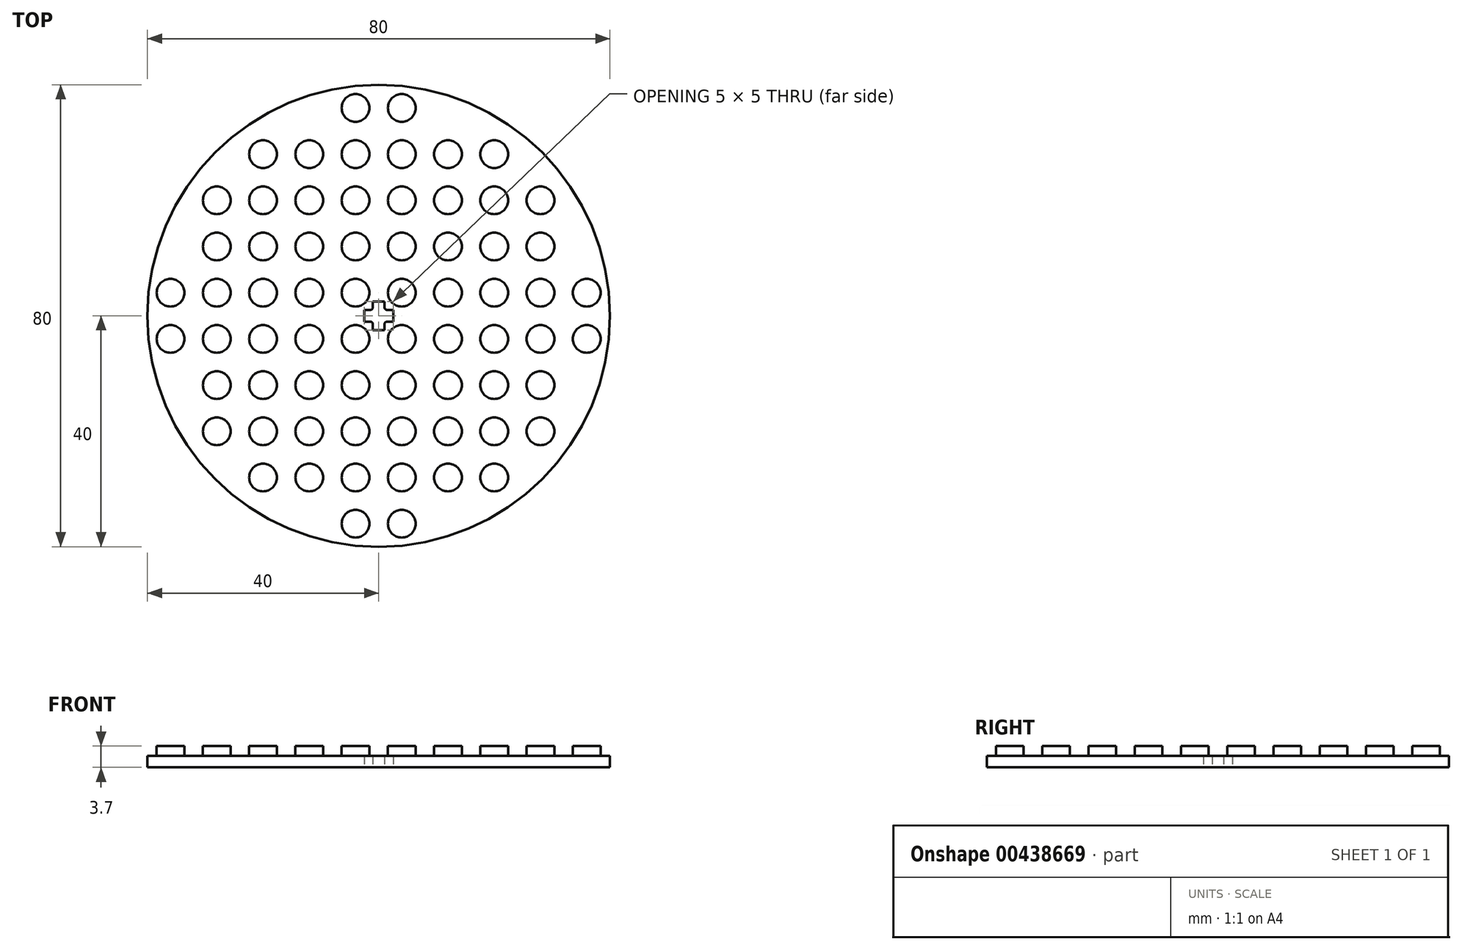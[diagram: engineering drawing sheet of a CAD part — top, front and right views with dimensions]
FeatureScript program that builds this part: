
annotation { "Feature Type Name" : "Feature", "Feature Type Description" : "" }
export const myFeature = defineFeature(function(context is Context, id is Id, definition is map)
    precondition{}
    {
        {
            var Q0;
            Q0=qCreatedBy(makeId("Top.planeOp"),FACE);
            var sketch = newSketch(context, id + "F0", { "sketchPlane" : qUnion([Q0])});
            skCircle(sketch, "E0", {"center": v(0, 0) * mm, "radius": 2.4 * mm});
            skCircle(sketch, "E1.0.1.0", {"center": v(0, 8) * mm, "radius": 2.4 * mm});
            skCircle(sketch, "E1.0.4.0", {"center": v(0, 32) * mm, "radius": 2.4 * mm});
            skCircle(sketch, "E1.0.5.0", {"center": v(0, 40) * mm, "radius": 2.4 * mm});
            skCircle(sketch, "E1.1.0.0", {"center": v(8, 0) * mm, "radius": 2.4 * mm});
            skCircle(sketch, "E1.1.2.0", {"center": v(8, 16) * mm, "radius": 2.4 * mm});
            skCircle(sketch, "E1.1.3.0", {"center": v(8, 24) * mm, "radius": 2.4 * mm});
            skCircle(sketch, "E1.1.4.0", {"center": v(8, 32) * mm, "radius": 2.4 * mm});
            skCircle(sketch, "E1.1.5.0", {"center": v(8, 40) * mm, "radius": 2.4 * mm});
            skCircle(sketch, "E1.1.6.0", {"center": v(8, 48) * mm, "radius": 2.4 * mm});
            skCircle(sketch, "E1.1.7.0", {"center": v(8, 56) * mm, "radius": 2.4 * mm});
            skCircle(sketch, "E1.2.1.0", {"center": v(16, 8) * mm, "radius": 2.4 * mm});
            skCircle(sketch, "E1.2.2.0", {"center": v(16, 16) * mm, "radius": 2.4 * mm});
            skCircle(sketch, "E1.2.3.0", {"center": v(16, 24) * mm, "radius": 2.4 * mm});
            skCircle(sketch, "E1.2.4.0", {"center": v(16, 32) * mm, "radius": 2.4 * mm});
            skCircle(sketch, "E1.2.5.0", {"center": v(16, 40) * mm, "radius": 2.4 * mm});
            skCircle(sketch, "E1.2.6.0", {"center": v(16, 48) * mm, "radius": 2.4 * mm});
            skCircle(sketch, "E1.2.7.0", {"center": v(16, 56) * mm, "radius": 2.4 * mm});
            skCircle(sketch, "E1.2.8.0", {"center": v(16, 64) * mm, "radius": 2.4 * mm});
            skCircle(sketch, "E1.3.1.0", {"center": v(24, 8) * mm, "radius": 2.4 * mm});
            skCircle(sketch, "E1.3.2.0", {"center": v(24, 16) * mm, "radius": 2.4 * mm});
            skCircle(sketch, "E1.3.3.0", {"center": v(24, 24) * mm, "radius": 2.4 * mm});
            skCircle(sketch, "E1.3.4.0", {"center": v(24, 32) * mm, "radius": 2.4 * mm});
            skCircle(sketch, "E1.3.5.0", {"center": v(24, 40) * mm, "radius": 2.4 * mm});
            skCircle(sketch, "E1.3.6.0", {"center": v(24, 48) * mm, "radius": 2.4 * mm});
            skCircle(sketch, "E1.3.7.0", {"center": v(24, 56) * mm, "radius": 2.4 * mm});
            skCircle(sketch, "E1.3.8.0", {"center": v(24, 64) * mm, "radius": 2.4 * mm});
            skCircle(sketch, "E1.4.0.0", {"center": v(32, 0) * mm, "radius": 2.4 * mm});
            skCircle(sketch, "E1.4.1.0", {"center": v(32, 8) * mm, "radius": 2.4 * mm});
            skCircle(sketch, "E1.4.2.0", {"center": v(32, 16) * mm, "radius": 2.4 * mm});
            skCircle(sketch, "E1.4.3.0", {"center": v(32, 24) * mm, "radius": 2.4 * mm});
            skCircle(sketch, "E1.4.4.0", {"center": v(32, 32) * mm, "radius": 2.4 * mm});
            skCircle(sketch, "E1.4.5.0", {"center": v(32, 40) * mm, "radius": 2.4 * mm});
            skCircle(sketch, "E1.4.6.0", {"center": v(32, 48) * mm, "radius": 2.4 * mm});
            skCircle(sketch, "E1.4.7.0", {"center": v(32, 56) * mm, "radius": 2.4 * mm});
            skCircle(sketch, "E1.4.8.0", {"center": v(32, 64) * mm, "radius": 2.4 * mm});
            skCircle(sketch, "E1.4.9.0", {"center": v(32, 72) * mm, "radius": 2.4 * mm});
            skCircle(sketch, "E1.5.0.0", {"center": v(40, 0) * mm, "radius": 2.4 * mm});
            skCircle(sketch, "E1.5.1.0", {"center": v(40, 8) * mm, "radius": 2.4 * mm});
            skCircle(sketch, "E1.5.2.0", {"center": v(40, 16) * mm, "radius": 2.4 * mm});
            skCircle(sketch, "E1.5.3.0", {"center": v(40, 24) * mm, "radius": 2.4 * mm});
            skCircle(sketch, "E1.5.4.0", {"center": v(40, 32) * mm, "radius": 2.4 * mm});
            skCircle(sketch, "E1.5.5.0", {"center": v(40, 40) * mm, "radius": 2.4 * mm});
            skCircle(sketch, "E1.5.6.0", {"center": v(40, 48) * mm, "radius": 2.4 * mm});
            skCircle(sketch, "E1.5.7.0", {"center": v(40, 56) * mm, "radius": 2.4 * mm});
            skCircle(sketch, "E1.5.8.0", {"center": v(40, 64) * mm, "radius": 2.4 * mm});
            skCircle(sketch, "E1.5.9.0", {"center": v(40, 72) * mm, "radius": 2.4 * mm});
            skCircle(sketch, "E1.6.1.0", {"center": v(48, 8) * mm, "radius": 2.4 * mm});
            skCircle(sketch, "E1.6.2.0", {"center": v(48, 16) * mm, "radius": 2.4 * mm});
            skCircle(sketch, "E1.6.3.0", {"center": v(48, 24) * mm, "radius": 2.4 * mm});
            skCircle(sketch, "E1.6.4.0", {"center": v(48, 32) * mm, "radius": 2.4 * mm});
            skCircle(sketch, "E1.6.5.0", {"center": v(48, 40) * mm, "radius": 2.4 * mm});
            skCircle(sketch, "E1.6.6.0", {"center": v(48, 48) * mm, "radius": 2.4 * mm});
            skCircle(sketch, "E1.6.7.0", {"center": v(48, 56) * mm, "radius": 2.4 * mm});
            skCircle(sketch, "E1.6.8.0", {"center": v(48, 64) * mm, "radius": 2.4 * mm});
            skCircle(sketch, "E1.7.1.0", {"center": v(56, 8) * mm, "radius": 2.4 * mm});
            skCircle(sketch, "E1.7.2.0", {"center": v(56, 16) * mm, "radius": 2.4 * mm});
            skCircle(sketch, "E1.7.3.0", {"center": v(56, 24) * mm, "radius": 2.4 * mm});
            skCircle(sketch, "E1.7.4.0", {"center": v(56, 32) * mm, "radius": 2.4 * mm});
            skCircle(sketch, "E1.7.5.0", {"center": v(56, 40) * mm, "radius": 2.4 * mm});
            skCircle(sketch, "E1.7.6.0", {"center": v(56, 48) * mm, "radius": 2.4 * mm});
            skCircle(sketch, "E1.7.7.0", {"center": v(56, 56) * mm, "radius": 2.4 * mm});
            skCircle(sketch, "E1.7.8.0", {"center": v(56, 64) * mm, "radius": 2.4 * mm});
            skCircle(sketch, "E1.8.2.0", {"center": v(64, 16) * mm, "radius": 2.4 * mm});
            skCircle(sketch, "E1.8.3.0", {"center": v(64, 24) * mm, "radius": 2.4 * mm});
            skCircle(sketch, "E1.8.4.0", {"center": v(64, 32) * mm, "radius": 2.4 * mm});
            skCircle(sketch, "E1.8.5.0", {"center": v(64, 40) * mm, "radius": 2.4 * mm});
            skCircle(sketch, "E1.8.6.0", {"center": v(64, 48) * mm, "radius": 2.4 * mm});
            skCircle(sketch, "E1.8.7.0", {"center": v(64, 56) * mm, "radius": 2.4 * mm});
            skCircle(sketch, "E1.9.4.0", {"center": v(72, 32) * mm, "radius": 2.4 * mm});
            skCircle(sketch, "E1.9.5.0", {"center": v(72, 40) * mm, "radius": 2.4 * mm});
            skLineSegment(sketch, "E1.direction1", {"start": v(0, 0) * mm, "end": v(8, 0) * mm, "construction": true});
            skLineSegment(sketch, "E1.direction2", {"start": v(0, 0) * mm, "end": v(0, 8) * mm, "construction": true});
            skLineSegment(sketch, "E2", {"start": v(40, 32) * mm, "end": v(32, 40) * mm, "construction": true});
            skLineSegment(sketch, "E3", {"start": v(40, 40) * mm, "end": v(32, 32) * mm, "construction": true});
            skCircle(sketch, "E4", {"center": v(36, 36) * mm, "radius": 40 * mm});
            skLineSegment(sketch, "E5.bottom", {"start": v(35, 33.5) * mm, "end": v(37, 33.5) * mm});
            skLineSegment(sketch, "E5.top", {"start": v(35, 38.5) * mm, "end": v(37, 38.5) * mm});
            skLineSegment(sketch, "E5.left", {"start": v(35, 33.5) * mm, "end": v(35, 38.5) * mm});
            skLineSegment(sketch, "E5.right", {"start": v(37, 33.5) * mm, "end": v(37, 38.5) * mm});
            skLineSegment(sketch, "E6.bottom", {"start": v(38.5, 35) * mm, "end": v(33.5, 35) * mm});
            skLineSegment(sketch, "E6.top", {"start": v(38.5, 37) * mm, "end": v(35, 37) * mm});
            skLineSegment(sketch, "E6.left", {"start": v(38.5, 35) * mm, "end": v(38.5, 37) * mm});
            skLineSegment(sketch, "E6.right", {"start": v(33.5, 35) * mm, "end": v(33.5, 37) * mm});
            skLineSegment(sketch, "E7", {"start": v(35, 37) * mm, "end": v(33.5, 37) * mm});
            skSolve(sketch);
        }
        {
            var Q0;
            Q0=makeQuery(id+"F0.imprint","IMPRINT",FACE,{"disambiguationData":[TD([[makeQuery(id+"F0.imprint","IMPRINT",EDGE,{"derivedFrom":sQuery(id+"F0.wireOp",EDGE,"E1.1.2.0")}),1.0]])]});
            var Q1;
            Q1=makeQuery(id+"F0.imprint","IMPRINT",FACE,{"disambiguationData":[TD([[makeQuery(id+"F0.imprint","IMPRINT",EDGE,{"derivedFrom":sQuery(id+"F0.wireOp",EDGE,"E1.2.1.0")}),1.0]])]});
            var Q2;
            Q2=makeQuery(id+"F0.imprint","IMPRINT",FACE,{"disambiguationData":[TD([[makeQuery(id+"F0.imprint","IMPRINT",EDGE,{"derivedFrom":sQuery(id+"F0.wireOp",EDGE,"E1.3.1.0")}),1.0]])]});
            var Q3;
            Q3=makeQuery(id+"F0.imprint","IMPRINT",FACE,{"disambiguationData":[TD([[makeQuery(id+"F0.imprint","IMPRINT",EDGE,{"derivedFrom":sQuery(id+"F0.wireOp",EDGE,"E1.2.2.0")}),1.0]])]});
            var Q4;
            Q4=makeQuery(id+"F0.imprint","IMPRINT",FACE,{"disambiguationData":[TD([[makeQuery(id+"F0.imprint","IMPRINT",EDGE,{"derivedFrom":sQuery(id+"F0.wireOp",EDGE,"E1.3.2.0")}),1.0]])]});
            var Q5;
            Q5=makeQuery(id+"F0.imprint","IMPRINT",FACE,{"disambiguationData":[TD([[makeQuery(id+"F0.imprint","IMPRINT",EDGE,{"derivedFrom":sQuery(id+"F0.wireOp",EDGE,"E1.4.0.0")}),1.0]])]});
            var Q6;
            Q6=makeQuery(id+"F0.imprint","IMPRINT",FACE,{"disambiguationData":[TD([[makeQuery(id+"F0.imprint","IMPRINT",EDGE,{"derivedFrom":sQuery(id+"F0.wireOp",EDGE,"E1.4.1.0")}),1.0]])]});
            var Q7;
            Q7=makeQuery(id+"F0.imprint","IMPRINT",FACE,{"disambiguationData":[TD([[makeQuery(id+"F0.imprint","IMPRINT",EDGE,{"derivedFrom":sQuery(id+"F0.wireOp",EDGE,"E1.4.2.0")}),1.0]])]});
            var Q8;
            Q8=makeQuery(id+"F0.imprint","IMPRINT",FACE,{"disambiguationData":[TD([[makeQuery(id+"F0.imprint","IMPRINT",EDGE,{"derivedFrom":sQuery(id+"F0.wireOp",EDGE,"E1.4.3.0")}),1.0]])]});
            var Q9;
            Q9=makeQuery(id+"F0.imprint","IMPRINT",FACE,{"disambiguationData":[TD([[makeQuery(id+"F0.imprint","IMPRINT",EDGE,{"derivedFrom":sQuery(id+"F0.wireOp",EDGE,"E1.3.3.0")}),1.0]])]});
            var Q10;
            Q10=makeQuery(id+"F0.imprint","IMPRINT",FACE,{"disambiguationData":[TD([[makeQuery(id+"F0.imprint","IMPRINT",EDGE,{"derivedFrom":sQuery(id+"F0.wireOp",EDGE,"E1.2.3.0")}),1.0]])]});
            var Q11;
            Q11=makeQuery(id+"F0.imprint","IMPRINT",FACE,{"disambiguationData":[TD([[makeQuery(id+"F0.imprint","IMPRINT",EDGE,{"derivedFrom":sQuery(id+"F0.wireOp",EDGE,"E1.1.3.0")}),1.0]])]});
            var Q12;
            Q12=makeQuery(id+"F0.imprint","IMPRINT",FACE,{"disambiguationData":[TD([[makeQuery(id+"F0.imprint","IMPRINT",EDGE,{"derivedFrom":sQuery(id+"F0.wireOp",EDGE,"E1.0.4.0")}),1.0]])]});
            var Q13;
            Q13=makeQuery(id+"F0.imprint","IMPRINT",FACE,{"disambiguationData":[TD([[makeQuery(id+"F0.imprint","IMPRINT",EDGE,{"derivedFrom":sQuery(id+"F0.wireOp",EDGE,"E1.1.4.0")}),1.0]])]});
            var Q14;
            Q14=makeQuery(id+"F0.imprint","IMPRINT",FACE,{"disambiguationData":[TD([[makeQuery(id+"F0.imprint","IMPRINT",EDGE,{"derivedFrom":sQuery(id+"F0.wireOp",EDGE,"E1.2.4.0")}),1.0]])]});
            var Q15;
            Q15=makeQuery(id+"F0.imprint","IMPRINT",FACE,{"disambiguationData":[TD([[makeQuery(id+"F0.imprint","IMPRINT",EDGE,{"derivedFrom":sQuery(id+"F0.wireOp",EDGE,"E1.3.4.0")}),1.0]])]});
            var Q16;
            Q16=makeQuery(id+"F0.imprint","IMPRINT",FACE,{"disambiguationData":[TD([[makeQuery(id+"F0.imprint","IMPRINT",EDGE,{"derivedFrom":sQuery(id+"F0.wireOp",EDGE,"E1.4.4.0")}),1.0]])]});
            var Q17;
            Q17=makeQuery(id+"F0.imprint","IMPRINT",FACE,{"disambiguationData":[TD([[makeQuery(id+"F0.imprint","IMPRINT",EDGE,{"derivedFrom":sQuery(id+"F0.wireOp",EDGE,"E1.4.5.0")}),1.0]])]});
            var Q18;
            Q18=makeQuery(id+"F0.imprint","IMPRINT",FACE,{"disambiguationData":[TD([[makeQuery(id+"F0.imprint","IMPRINT",EDGE,{"derivedFrom":sQuery(id+"F0.wireOp",EDGE,"E1.3.5.0")}),1.0]])]});
            var Q19;
            Q19=makeQuery(id+"F0.imprint","IMPRINT",FACE,{"disambiguationData":[TD([[makeQuery(id+"F0.imprint","IMPRINT",EDGE,{"derivedFrom":sQuery(id+"F0.wireOp",EDGE,"E1.2.5.0")}),1.0]])]});
            var Q20;
            Q20=makeQuery(id+"F0.imprint","IMPRINT",FACE,{"disambiguationData":[TD([[makeQuery(id+"F0.imprint","IMPRINT",EDGE,{"derivedFrom":sQuery(id+"F0.wireOp",EDGE,"E1.1.5.0")}),1.0]])]});
            var Q21;
            Q21=makeQuery(id+"F0.imprint","IMPRINT",FACE,{"disambiguationData":[TD([[makeQuery(id+"F0.imprint","IMPRINT",EDGE,{"derivedFrom":sQuery(id+"F0.wireOp",EDGE,"E1.0.5.0")}),1.0]])]});
            var Q22;
            Q22=makeQuery(id+"F0.imprint","IMPRINT",FACE,{"disambiguationData":[TD([[makeQuery(id+"F0.imprint","IMPRINT",EDGE,{"derivedFrom":sQuery(id+"F0.wireOp",EDGE,"E1.1.6.0")}),1.0]])]});
            var Q23;
            Q23=makeQuery(id+"F0.imprint","IMPRINT",FACE,{"disambiguationData":[TD([[makeQuery(id+"F0.imprint","IMPRINT",EDGE,{"derivedFrom":sQuery(id+"F0.wireOp",EDGE,"E1.2.6.0")}),1.0]])]});
            var Q24;
            Q24=makeQuery(id+"F0.imprint","IMPRINT",FACE,{"disambiguationData":[TD([[makeQuery(id+"F0.imprint","IMPRINT",EDGE,{"derivedFrom":sQuery(id+"F0.wireOp",EDGE,"E1.4.6.0")}),1.0]])]});
            var Q25;
            Q25=makeQuery(id+"F0.imprint","IMPRINT",FACE,{"disambiguationData":[TD([[makeQuery(id+"F0.imprint","IMPRINT",EDGE,{"derivedFrom":sQuery(id+"F0.wireOp",EDGE,"E1.4.7.0")}),1.0]])]});
            var Q26;
            Q26=makeQuery(id+"F0.imprint","IMPRINT",FACE,{"disambiguationData":[TD([[makeQuery(id+"F0.imprint","IMPRINT",EDGE,{"derivedFrom":sQuery(id+"F0.wireOp",EDGE,"E1.3.7.0")}),1.0]])]});
            var Q27;
            Q27=makeQuery(id+"F0.imprint","IMPRINT",FACE,{"disambiguationData":[TD([[makeQuery(id+"F0.imprint","IMPRINT",EDGE,{"derivedFrom":sQuery(id+"F0.wireOp",EDGE,"E1.2.7.0")}),1.0]])]});
            var Q28;
            Q28=makeQuery(id+"F0.imprint","IMPRINT",FACE,{"disambiguationData":[TD([[makeQuery(id+"F0.imprint","IMPRINT",EDGE,{"derivedFrom":sQuery(id+"F0.wireOp",EDGE,"E1.1.7.0")}),1.0]])]});
            var Q29;
            Q29=makeQuery(id+"F0.imprint","IMPRINT",FACE,{"disambiguationData":[TD([[makeQuery(id+"F0.imprint","IMPRINT",EDGE,{"derivedFrom":sQuery(id+"F0.wireOp",EDGE,"E1.3.6.0")}),1.0]])]});
            var Q30;
            Q30=makeQuery(id+"F0.imprint","IMPRINT",FACE,{"disambiguationData":[TD([[makeQuery(id+"F0.imprint","IMPRINT",EDGE,{"derivedFrom":sQuery(id+"F0.wireOp",EDGE,"E1.2.8.0")}),1.0]])]});
            var Q31;
            Q31=makeQuery(id+"F0.imprint","IMPRINT",FACE,{"disambiguationData":[TD([[makeQuery(id+"F0.imprint","IMPRINT",EDGE,{"derivedFrom":sQuery(id+"F0.wireOp",EDGE,"E1.3.8.0")}),1.0]])]});
            var Q32;
            Q32=makeQuery(id+"F0.imprint","IMPRINT",FACE,{"disambiguationData":[TD([[makeQuery(id+"F0.imprint","IMPRINT",EDGE,{"derivedFrom":sQuery(id+"F0.wireOp",EDGE,"E1.4.8.0")}),1.0]])]});
            var Q33;
            Q33=makeQuery(id+"F0.imprint","IMPRINT",FACE,{"disambiguationData":[TD([[makeQuery(id+"F0.imprint","IMPRINT",EDGE,{"derivedFrom":sQuery(id+"F0.wireOp",EDGE,"E1.4.9.0")}),1.0]])]});
            var Q34;
            Q34=makeQuery(id+"F0.imprint","IMPRINT",FACE,{"disambiguationData":[TD([[makeQuery(id+"F0.imprint","IMPRINT",EDGE,{"derivedFrom":sQuery(id+"F0.wireOp",EDGE,"E1.5.9.0")}),1.0]])]});
            var Q35;
            Q35=makeQuery(id+"F0.imprint","IMPRINT",FACE,{"disambiguationData":[TD([[makeQuery(id+"F0.imprint","IMPRINT",EDGE,{"derivedFrom":sQuery(id+"F0.wireOp",EDGE,"E1.5.8.0")}),1.0]])]});
            var Q36;
            Q36=makeQuery(id+"F0.imprint","IMPRINT",FACE,{"disambiguationData":[TD([[makeQuery(id+"F0.imprint","IMPRINT",EDGE,{"derivedFrom":sQuery(id+"F0.wireOp",EDGE,"E1.5.7.0")}),1.0]])]});
            var Q37;
            Q37=makeQuery(id+"F0.imprint","IMPRINT",FACE,{"disambiguationData":[TD([[makeQuery(id+"F0.imprint","IMPRINT",EDGE,{"derivedFrom":sQuery(id+"F0.wireOp",EDGE,"E1.5.6.0")}),1.0]])]});
            var Q38;
            Q38=makeQuery(id+"F0.imprint","IMPRINT",FACE,{"disambiguationData":[TD([[makeQuery(id+"F0.imprint","IMPRINT",EDGE,{"derivedFrom":sQuery(id+"F0.wireOp",EDGE,"E1.5.5.0")}),1.0]])]});
            var Q39;
            Q39=makeQuery(id+"F0.imprint","IMPRINT",FACE,{"disambiguationData":[TD([[makeQuery(id+"F0.imprint","IMPRINT",EDGE,{"derivedFrom":sQuery(id+"F0.wireOp",EDGE,"E1.5.4.0")}),1.0]])]});
            var Q40;
            Q40=makeQuery(id+"F0.imprint","IMPRINT",FACE,{"disambiguationData":[TD([[makeQuery(id+"F0.imprint","IMPRINT",EDGE,{"derivedFrom":sQuery(id+"F0.wireOp",EDGE,"E1.5.3.0")}),1.0]])]});
            var Q41;
            Q41=makeQuery(id+"F0.imprint","IMPRINT",FACE,{"disambiguationData":[TD([[makeQuery(id+"F0.imprint","IMPRINT",EDGE,{"derivedFrom":sQuery(id+"F0.wireOp",EDGE,"E1.5.2.0")}),1.0]])]});
            var Q42;
            Q42=makeQuery(id+"F0.imprint","IMPRINT",FACE,{"disambiguationData":[TD([[makeQuery(id+"F0.imprint","IMPRINT",EDGE,{"derivedFrom":sQuery(id+"F0.wireOp",EDGE,"E1.5.1.0")}),1.0]])]});
            var Q43;
            Q43=makeQuery(id+"F0.imprint","IMPRINT",FACE,{"disambiguationData":[TD([[makeQuery(id+"F0.imprint","IMPRINT",EDGE,{"derivedFrom":sQuery(id+"F0.wireOp",EDGE,"E1.5.0.0")}),1.0]])]});
            var Q44;
            Q44=makeQuery(id+"F0.imprint","IMPRINT",FACE,{"disambiguationData":[TD([[makeQuery(id+"F0.imprint","IMPRINT",EDGE,{"derivedFrom":sQuery(id+"F0.wireOp",EDGE,"E1.6.1.0")}),1.0]])]});
            var Q45;
            Q45=makeQuery(id+"F0.imprint","IMPRINT",FACE,{"disambiguationData":[TD([[makeQuery(id+"F0.imprint","IMPRINT",EDGE,{"derivedFrom":sQuery(id+"F0.wireOp",EDGE,"E1.6.2.0")}),1.0]])]});
            var Q46;
            Q46=makeQuery(id+"F0.imprint","IMPRINT",FACE,{"disambiguationData":[TD([[makeQuery(id+"F0.imprint","IMPRINT",EDGE,{"derivedFrom":sQuery(id+"F0.wireOp",EDGE,"E1.6.3.0")}),1.0]])]});
            var Q47;
            Q47=makeQuery(id+"F0.imprint","IMPRINT",FACE,{"disambiguationData":[TD([[makeQuery(id+"F0.imprint","IMPRINT",EDGE,{"derivedFrom":sQuery(id+"F0.wireOp",EDGE,"E1.6.4.0")}),1.0]])]});
            var Q48;
            Q48=makeQuery(id+"F0.imprint","IMPRINT",FACE,{"disambiguationData":[TD([[makeQuery(id+"F0.imprint","IMPRINT",EDGE,{"derivedFrom":sQuery(id+"F0.wireOp",EDGE,"E1.6.5.0")}),1.0]])]});
            var Q49;
            Q49=makeQuery(id+"F0.imprint","IMPRINT",FACE,{"disambiguationData":[TD([[makeQuery(id+"F0.imprint","IMPRINT",EDGE,{"derivedFrom":sQuery(id+"F0.wireOp",EDGE,"E1.6.6.0")}),1.0]])]});
            var Q50;
            Q50=makeQuery(id+"F0.imprint","IMPRINT",FACE,{"disambiguationData":[TD([[makeQuery(id+"F0.imprint","IMPRINT",EDGE,{"derivedFrom":sQuery(id+"F0.wireOp",EDGE,"E1.6.7.0")}),1.0]])]});
            var Q51;
            Q51=makeQuery(id+"F0.imprint","IMPRINT",FACE,{"disambiguationData":[TD([[makeQuery(id+"F0.imprint","IMPRINT",EDGE,{"derivedFrom":sQuery(id+"F0.wireOp",EDGE,"E1.6.8.0")}),1.0]])]});
            var Q52;
            Q52=makeQuery(id+"F0.imprint","IMPRINT",FACE,{"disambiguationData":[TD([[makeQuery(id+"F0.imprint","IMPRINT",EDGE,{"derivedFrom":sQuery(id+"F0.wireOp",EDGE,"E1.7.8.0")}),1.0]])]});
            var Q53;
            Q53=makeQuery(id+"F0.imprint","IMPRINT",FACE,{"disambiguationData":[TD([[makeQuery(id+"F0.imprint","IMPRINT",EDGE,{"derivedFrom":sQuery(id+"F0.wireOp",EDGE,"E1.7.7.0")}),1.0]])]});
            var Q54;
            Q54=makeQuery(id+"F0.imprint","IMPRINT",FACE,{"disambiguationData":[TD([[makeQuery(id+"F0.imprint","IMPRINT",EDGE,{"derivedFrom":sQuery(id+"F0.wireOp",EDGE,"E1.7.6.0")}),1.0]])]});
            var Q55;
            Q55=makeQuery(id+"F0.imprint","IMPRINT",FACE,{"disambiguationData":[TD([[makeQuery(id+"F0.imprint","IMPRINT",EDGE,{"derivedFrom":sQuery(id+"F0.wireOp",EDGE,"E1.7.5.0")}),1.0]])]});
            var Q56;
            Q56=makeQuery(id+"F0.imprint","IMPRINT",FACE,{"disambiguationData":[TD([[makeQuery(id+"F0.imprint","IMPRINT",EDGE,{"derivedFrom":sQuery(id+"F0.wireOp",EDGE,"E1.7.4.0")}),1.0]])]});
            var Q57;
            Q57=makeQuery(id+"F0.imprint","IMPRINT",FACE,{"disambiguationData":[TD([[makeQuery(id+"F0.imprint","IMPRINT",EDGE,{"derivedFrom":sQuery(id+"F0.wireOp",EDGE,"E1.7.3.0")}),1.0]])]});
            var Q58;
            Q58=makeQuery(id+"F0.imprint","IMPRINT",FACE,{"disambiguationData":[TD([[makeQuery(id+"F0.imprint","IMPRINT",EDGE,{"derivedFrom":sQuery(id+"F0.wireOp",EDGE,"E1.7.2.0")}),1.0]])]});
            var Q59;
            Q59=makeQuery(id+"F0.imprint","IMPRINT",FACE,{"disambiguationData":[TD([[makeQuery(id+"F0.imprint","IMPRINT",EDGE,{"derivedFrom":sQuery(id+"F0.wireOp",EDGE,"E1.7.1.0")}),1.0]])]});
            var Q60;
            Q60=makeQuery(id+"F0.imprint","IMPRINT",FACE,{"disambiguationData":[TD([[makeQuery(id+"F0.imprint","IMPRINT",EDGE,{"derivedFrom":sQuery(id+"F0.wireOp",EDGE,"E1.8.2.0")}),1.0]])]});
            var Q61;
            Q61=makeQuery(id+"F0.imprint","IMPRINT",FACE,{"disambiguationData":[TD([[makeQuery(id+"F0.imprint","IMPRINT",EDGE,{"derivedFrom":sQuery(id+"F0.wireOp",EDGE,"E1.8.3.0")}),1.0]])]});
            var Q62;
            Q62=makeQuery(id+"F0.imprint","IMPRINT",FACE,{"disambiguationData":[TD([[makeQuery(id+"F0.imprint","IMPRINT",EDGE,{"derivedFrom":sQuery(id+"F0.wireOp",EDGE,"E1.8.4.0")}),1.0]])]});
            var Q63;
            Q63=makeQuery(id+"F0.imprint","IMPRINT",FACE,{"disambiguationData":[TD([[makeQuery(id+"F0.imprint","IMPRINT",EDGE,{"derivedFrom":sQuery(id+"F0.wireOp",EDGE,"E1.8.5.0")}),1.0]])]});
            var Q64;
            Q64=makeQuery(id+"F0.imprint","IMPRINT",FACE,{"disambiguationData":[TD([[makeQuery(id+"F0.imprint","IMPRINT",EDGE,{"derivedFrom":sQuery(id+"F0.wireOp",EDGE,"E1.8.6.0")}),1.0]])]});
            var Q65;
            Q65=makeQuery(id+"F0.imprint","IMPRINT",FACE,{"disambiguationData":[TD([[makeQuery(id+"F0.imprint","IMPRINT",EDGE,{"derivedFrom":sQuery(id+"F0.wireOp",EDGE,"E1.8.7.0")}),1.0]])]});
            var Q66;
            Q66=makeQuery(id+"F0.imprint","IMPRINT",FACE,{"disambiguationData":[TD([[makeQuery(id+"F0.imprint","IMPRINT",EDGE,{"derivedFrom":sQuery(id+"F0.wireOp",EDGE,"E1.9.5.0")}),1.0]])]});
            var Q67;
            Q67=makeQuery(id+"F0.imprint","IMPRINT",FACE,{"disambiguationData":[TD([[makeQuery(id+"F0.imprint","IMPRINT",EDGE,{"derivedFrom":sQuery(id+"F0.wireOp",EDGE,"E1.9.4.0")}),1.0]])]});
            extrude(context, id + "F1", {"entities" : qUnion([Q0, Q1, Q2, Q3, Q4, Q5, Q6, Q7, Q8, Q9, Q10, Q11, Q12, Q13, Q14, Q15, Q16, Q17, Q18, Q19, Q20, Q21, Q22, Q23, Q24, Q25, Q26, Q27, Q28, Q29, Q30, Q31, Q32, Q33, Q34, Q35, Q36, Q37, Q38, Q39, Q40, Q41, Q42, Q43, Q44, Q45, Q46, Q47, Q48, Q49, Q50, Q51, Q52, Q53, Q54, Q55, Q56, Q57, Q58, Q59, Q60, Q61, Q62, Q63, Q64, Q65, Q66, Q67]), "depth" : (1.7 + 2) * mm});
        }
        {
            var Q0;
            Q0=makeQuery(id+"F0.imprint","IMPRINT",FACE,{"disambiguationData":[TD([[makeQuery(id+"F0.imprint","IMPRINT",EDGE,{"derivedFrom":sQuery(id+"F0.wireOp",EDGE,"E1.0.4.0")}),-1.0]])]});
            extrude(context, id + "F2", {"entities" : qUnion([Q0]), "operationType" : NewBodyOperationType.ADD, "depth" : 2 * mm});
        }
        {
            var Q0;
            Q0=makeQuery(id+"F2.opExtrude","SWEPT_EDGE",EDGE,{"disambiguationData":[OSD([sQuery(id+"F0.wireOp",EDGE,"E5.right"),sQuery(id+"F0.wireOp",EDGE,"E6.bottom")])]});
            var Q1;
            Q1=makeQuery(id+"F2.opExtrude","SWEPT_EDGE",EDGE,{"disambiguationData":[OSD([sQuery(id+"F0.wireOp",EDGE,"E5.right"),sQuery(id+"F0.wireOp",EDGE,"E6.top")])]});
            var Q2;
            Q2=makeQuery(id+"F2.opExtrude","SWEPT_EDGE",EDGE,{"disambiguationData":[OSD([sQuery(id+"F0.wireOp",EDGE,"E5.left"),sQuery(id+"F0.wireOp",EDGE,"E6.top"),sQuery(id+"F0.wireOp",EDGE,"E7")])]});
            var Q3;
            Q3=makeQuery(id+"F2.opExtrude","SWEPT_EDGE",EDGE,{"disambiguationData":[OSD([sQuery(id+"F0.wireOp",EDGE,"E5.left"),sQuery(id+"F0.wireOp",EDGE,"E6.bottom")])]});
            fillet(context, id + "F3", {"entities" : qUnion([Q0, Q1, Q2, Q3]), "radius" : .5 * mm, "tangentPropagation" : true, "allowEdgeOverflow" : false});
        }
    });
